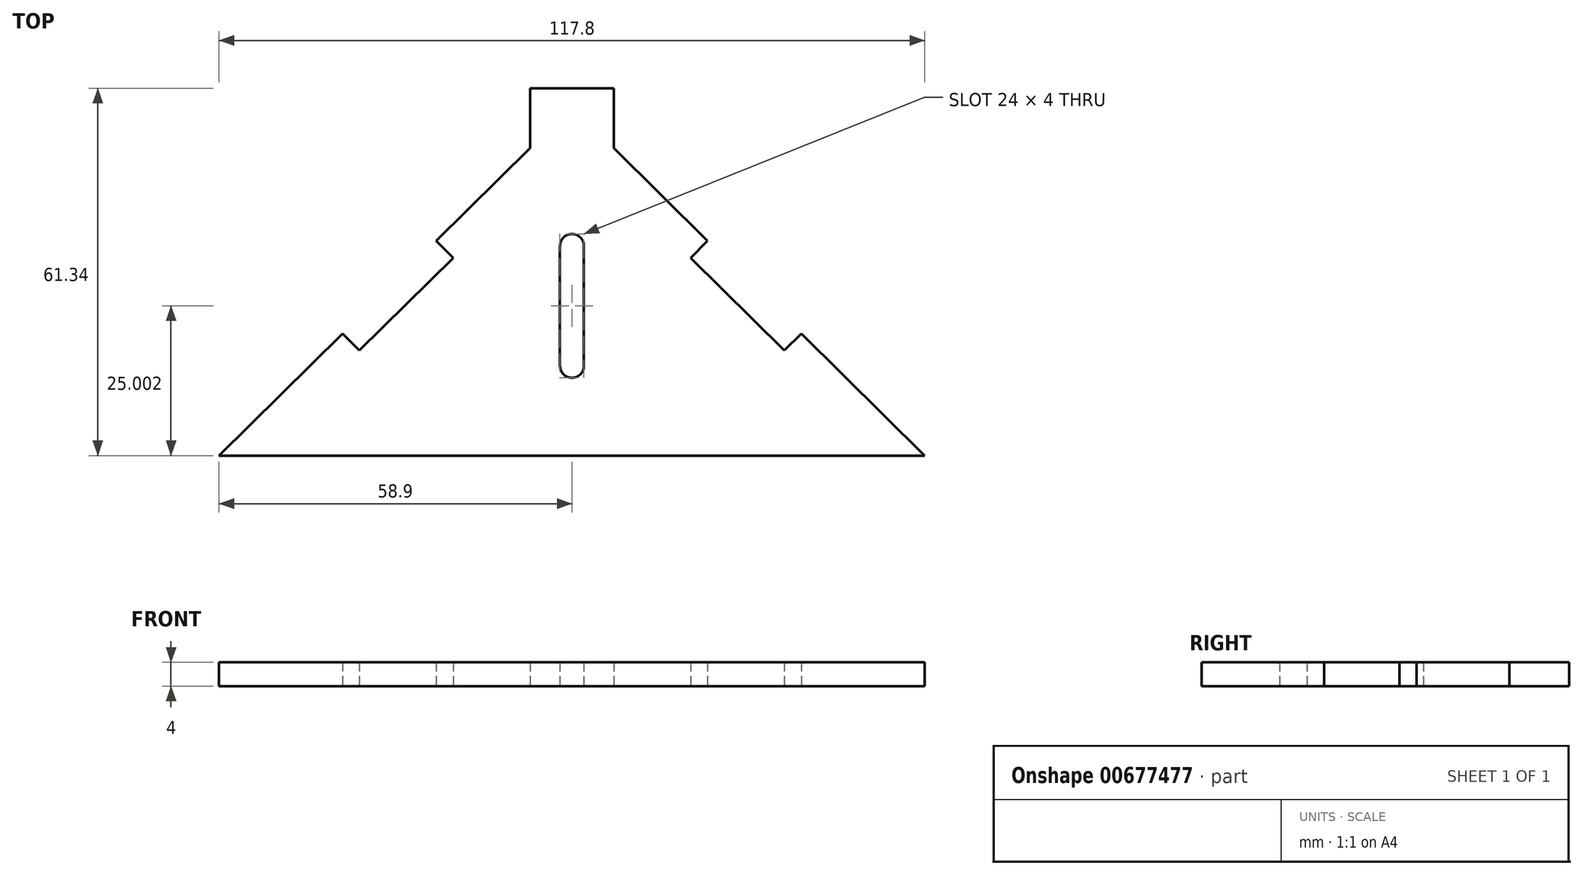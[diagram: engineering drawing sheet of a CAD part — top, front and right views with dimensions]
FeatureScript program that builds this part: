
annotation { "Feature Type Name" : "Feature", "Feature Type Description" : "" }
export const myFeature = defineFeature(function(context is Context, id is Id, definition is map)
    precondition{}
    {
        {
            var Q0;
            Q0=qCreatedBy(makeId("Top.planeOp"),FACE);
            var sketch = newSketch(context, id + "F0", { "sketchPlane" : qUnion([Q0])});
            skLineSegment(sketch, "E0", {"start": v(-21.83, 25.05) * mm, "end": v(-24.64, 27.89) * mm});
            skLineSegment(sketch, "E1", {"start": v(-9, 43.36) * mm, "end": v(-9, 53.36) * mm});
            skLineSegment(sketch, "E2", {"start": v(-9, 53.36) * mm, "end": v(5, 53.36) * mm});
            skLineSegment(sketch, "E3", {"start": v(5, 53.36) * mm, "end": v(5, 43.36) * mm});
            skLineSegment(sketch, "E4", {"start": v(-21.83, 25.05) * mm, "end": v(-37.47, 9.57) * mm});
            skLineSegment(sketch, "E5", {"start": v(-37.47, 9.57) * mm, "end": v(-40.28, 12.42) * mm});
            skLineSegment(sketch, "E6", {"start": v(-9, 43.36) * mm, "end": v(-24.64, 27.89) * mm});
            skLineSegment(sketch, "E7", {"start": v(-40.28, 12.42) * mm, "end": v(-60.9, -7.98) * mm});
            skLineSegment(sketch, "E8", {"start": v(17.83, 25.05) * mm, "end": v(20.64, 27.89) * mm});
            skLineSegment(sketch, "E9", {"start": v(20.64, 27.89) * mm, "end": v(17.83, 25.05) * mm});
            skLineSegment(sketch, "E10", {"start": v(17.83, 25.05) * mm, "end": v(33.47, 9.57) * mm});
            skLineSegment(sketch, "E11", {"start": v(33.47, 9.57) * mm, "end": v(36.28, 12.42) * mm});
            skLineSegment(sketch, "E12", {"start": v(5, 43.36) * mm, "end": v(20.64, 27.89) * mm});
            skLineSegment(sketch, "E13", {"start": v(36.28, 12.42) * mm, "end": v(56.9, -7.98) * mm});
            skLineSegment(sketch, "E14", {"start": v(-60.9, -7.98) * mm, "end": v(56.9, -7.98) * mm});
            skLineSegment(sketch, "E15", {"start": v(0, 7.02) * mm, "end": v(0, 27.02) * mm});
            skLineSegment(sketch, "E16", {"start": v(-4, 27.02) * mm, "end": v(-4, 7.02) * mm});
            skArc(sketch, "E17", {"start": v(0, 27.02) * mm, "mid": v(-2, 29.02) * mm, "end": v(-4, 27.02) * mm});
            skArc(sketch, "E18", {"start": v(-4, 7.02) * mm, "mid": v(-2, 5.02) * mm, "end": v(0, 7.02) * mm});
            skSolve(sketch);
        }
        {
            var Q0;
            Q0=makeQuery(id+"F0.imprint","IMPRINT",FACE,{"disambiguationData":[TD([[makeQuery(id+"F0.imprint","IMPRINT",EDGE,{"derivedFrom":sQuery(id+"F0.wireOp",EDGE,"E0")}),-1.0]])]});
            extrude(context, id + "F1", {"entities" : qUnion([Q0]), "depth" : 4 * mm, "offsetDistance" : 25 * mm});
        }
    });
